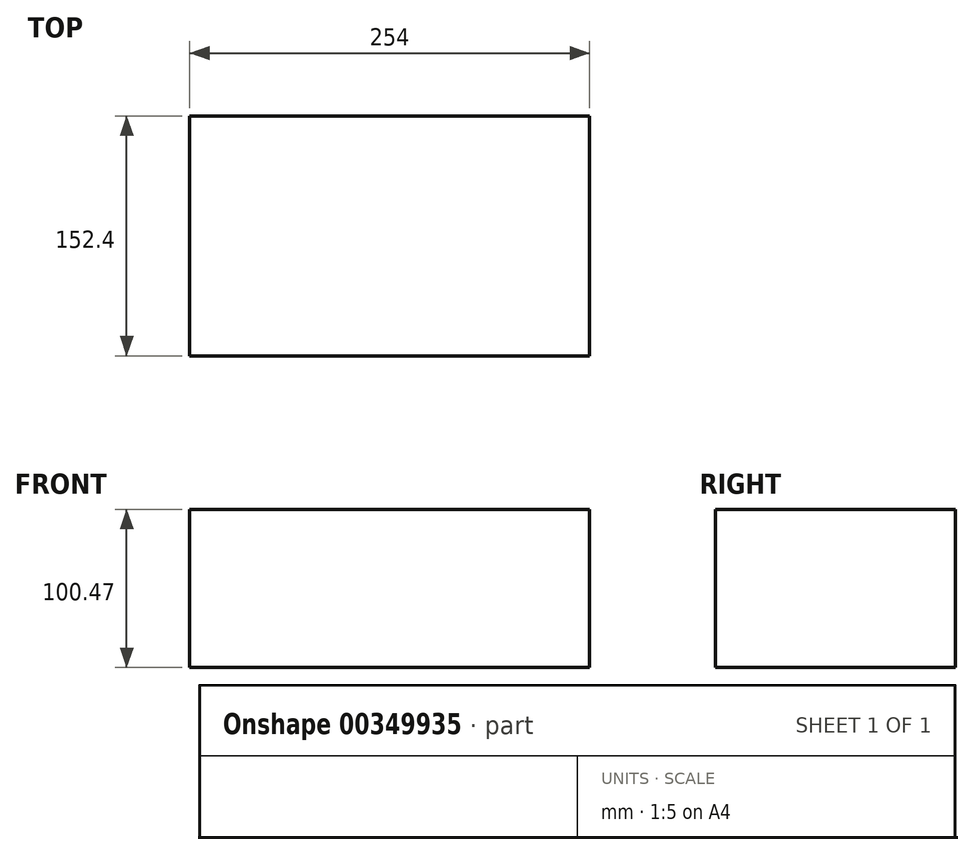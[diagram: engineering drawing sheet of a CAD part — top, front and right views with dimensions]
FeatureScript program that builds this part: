
annotation { "Feature Type Name" : "Feature", "Feature Type Description" : "" }
export const myFeature = defineFeature(function(context is Context, id is Id, definition is map)
    precondition{}
    {
        {
            var Q0;
            Q0=qCreatedBy(makeId("Front.planeOp"),FACE);
            var sketch = newSketch(context, id + "F0", { "sketchPlane" : qUnion([Q0])});
            skLineSegment(sketch, "E0.bottom", {"start": v(-86.33, 48.24) * mm, "end": v(167.67, 48.24) * mm});
            skLineSegment(sketch, "E0.top", {"start": v(-86.33, -52.23) * mm, "end": v(167.67, -52.23) * mm});
            skLineSegment(sketch, "E0.left", {"start": v(-86.33, 48.24) * mm, "end": v(-86.33, -52.23) * mm});
            skLineSegment(sketch, "E0.right", {"start": v(167.67, 48.24) * mm, "end": v(167.67, -52.23) * mm});
            skSolve(sketch);
        }
        {
            var Q0;
            Q0 = qSketchRegion(id + "F0", true);
            extrude(context, id + "F1", {"entities" : qUnion([Q0]), "depth" : 152.4 * mm, "offsetDistance" : 25.4 * mm});
        }
    });
